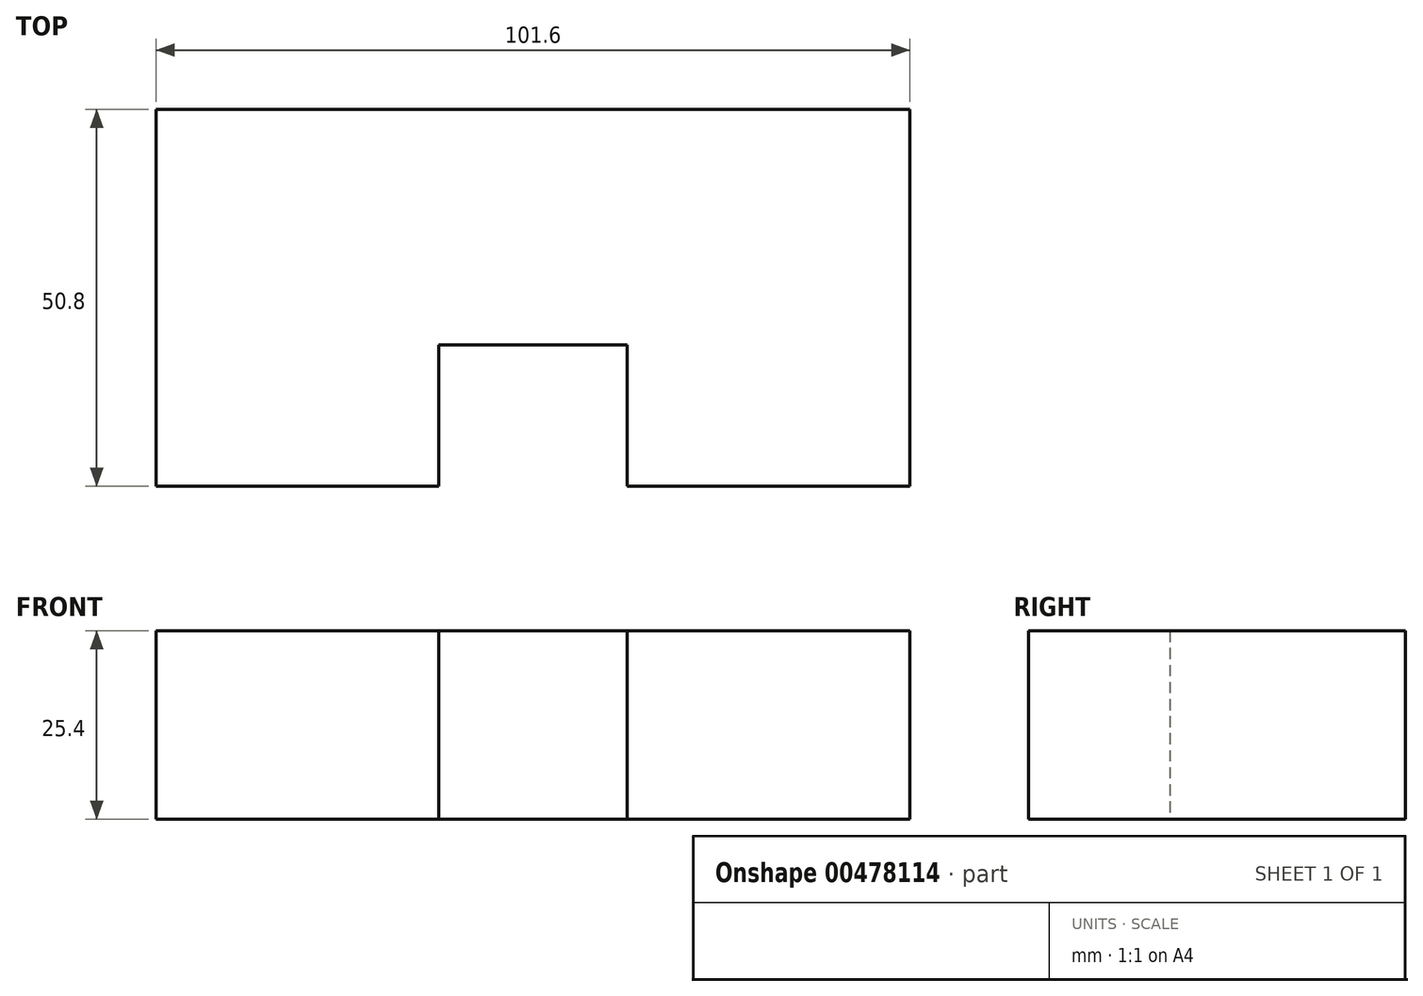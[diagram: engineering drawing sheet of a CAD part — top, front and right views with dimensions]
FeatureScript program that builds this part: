
annotation { "Feature Type Name" : "Feature", "Feature Type Description" : "" }
export const myFeature = defineFeature(function(context is Context, id is Id, definition is map)
    precondition{}
    {
        {
            var Q0;
            Q0=qCreatedBy(makeId("Top.planeOp"),FACE);
            var sketch = newSketch(context, id + "F0", { "sketchPlane" : qUnion([Q0])});
            skLineSegment(sketch, "E0", {"start": v(0, 0) * mm, "end": v(38.1, 0) * mm});
            skLineSegment(sketch, "E1", {"start": v(38.1, 0) * mm, "end": v(38.1, 19.05) * mm});
            skLineSegment(sketch, "E2", {"start": v(38.1, 19.05) * mm, "end": v(63.5, 19.05) * mm});
            skLineSegment(sketch, "E3", {"start": v(63.5, 19.05) * mm, "end": v(63.5, 0) * mm});
            skLineSegment(sketch, "E4", {"start": v(63.5, 0) * mm, "end": v(101.6, 0) * mm});
            skLineSegment(sketch, "E5", {"start": v(101.6, 0) * mm, "end": v(101.6, 50.8) * mm});
            skLineSegment(sketch, "E6", {"start": v(101.6, 50.8) * mm, "end": v(0, 50.8) * mm});
            skLineSegment(sketch, "E7", {"start": v(0, 50.8) * mm, "end": v(0, 0) * mm});
            skSolve(sketch);
        }
        {
            var Q0;
            Q0 = qSketchRegion(id + "F0", true);
            extrude(context, id + "F1", {"entities" : qUnion([Q0]), "depth" : 25.4 * mm});
        }
        {
            var Q0;
            Q0=makeQuery(id+"F1.opExtrude","CAP_FACE",FACE,{"disambiguationData":[OSD([sQuery(id+"F0.wireOp",EDGE,"E0"),sQuery(id+"F0.wireOp",EDGE,"E1"),sQuery(id+"F0.wireOp",EDGE,"E2"),sQuery(id+"F0.wireOp",EDGE,"E3"),sQuery(id+"F0.wireOp",EDGE,"E4"),sQuery(id+"F0.wireOp",EDGE,"E5"),sQuery(id+"F0.wireOp",EDGE,"E6"),sQuery(id+"F0.wireOp",EDGE,"E7")])],"isStart":false});
            var sketch = newSketch(context, id + "F2", { "sketchPlane" : qUnion([Q0])});
            skSolve(sketch);
        }
        {
            var Q0;
            Q0=makeQuery(id+"F1.opExtrude","CAP_FACE",FACE,{"disambiguationData":[OSD([sQuery(id+"F0.wireOp",EDGE,"E0"),sQuery(id+"F0.wireOp",EDGE,"E1"),sQuery(id+"F0.wireOp",EDGE,"E2"),sQuery(id+"F0.wireOp",EDGE,"E3"),sQuery(id+"F0.wireOp",EDGE,"E4"),sQuery(id+"F0.wireOp",EDGE,"E5"),sQuery(id+"F0.wireOp",EDGE,"E6"),sQuery(id+"F0.wireOp",EDGE,"E7")])],"isStart":false});
            var sketch = newSketch(context, id + "F3", { "sketchPlane" : qUnion([Q0])});
            skLineSegment(sketch, "E8", {"start": v(25.4, 50.8) * mm, "end": v(25.4, 31.75) * mm});
            skLineSegment(sketch, "E9", {"start": v(25.4, 31.75) * mm, "end": v(76.2, 31.75) * mm});
            skLineSegment(sketch, "E10", {"start": v(76.2, 31.75) * mm, "end": v(76.2, 50.8) * mm});
            skSolve(sketch);
        }
        {
            var Q0;
            Q0=makeQuery(id+"F2.imprint","IMPRINT",FACE,{"disambiguationData":[TD([[makeQuery(id+"F2.imprint","IMPRINT",EDGE,{"derivedFrom":makeQuery(id+"F1.opExtrude","CAP_EDGE",EDGE,{"disambiguationData":[OSD([sQuery(id+"F0.wireOp",EDGE,"E0")])],"isStart":false})}),1.0]])]});
            var Q1;
            Q1=sQuery(id+"F3.wireOp",EDGE,"E8");
            var Q2;
            Q2=sQuery(id+"F3.wireOp",EDGE,"E10");
            var Q3;
            Q3=sQuery(id+"F3.wireOp",EDGE,"E9");
            extrude(context, id + "F4", {"entities" : qUnion([Q0]), "bodyType" : ToolBodyType.SURFACE, "surfaceEntities" : qUnion([Q1, Q2, Q3]), "depth" : 38.1 * mm});
        }
    });
